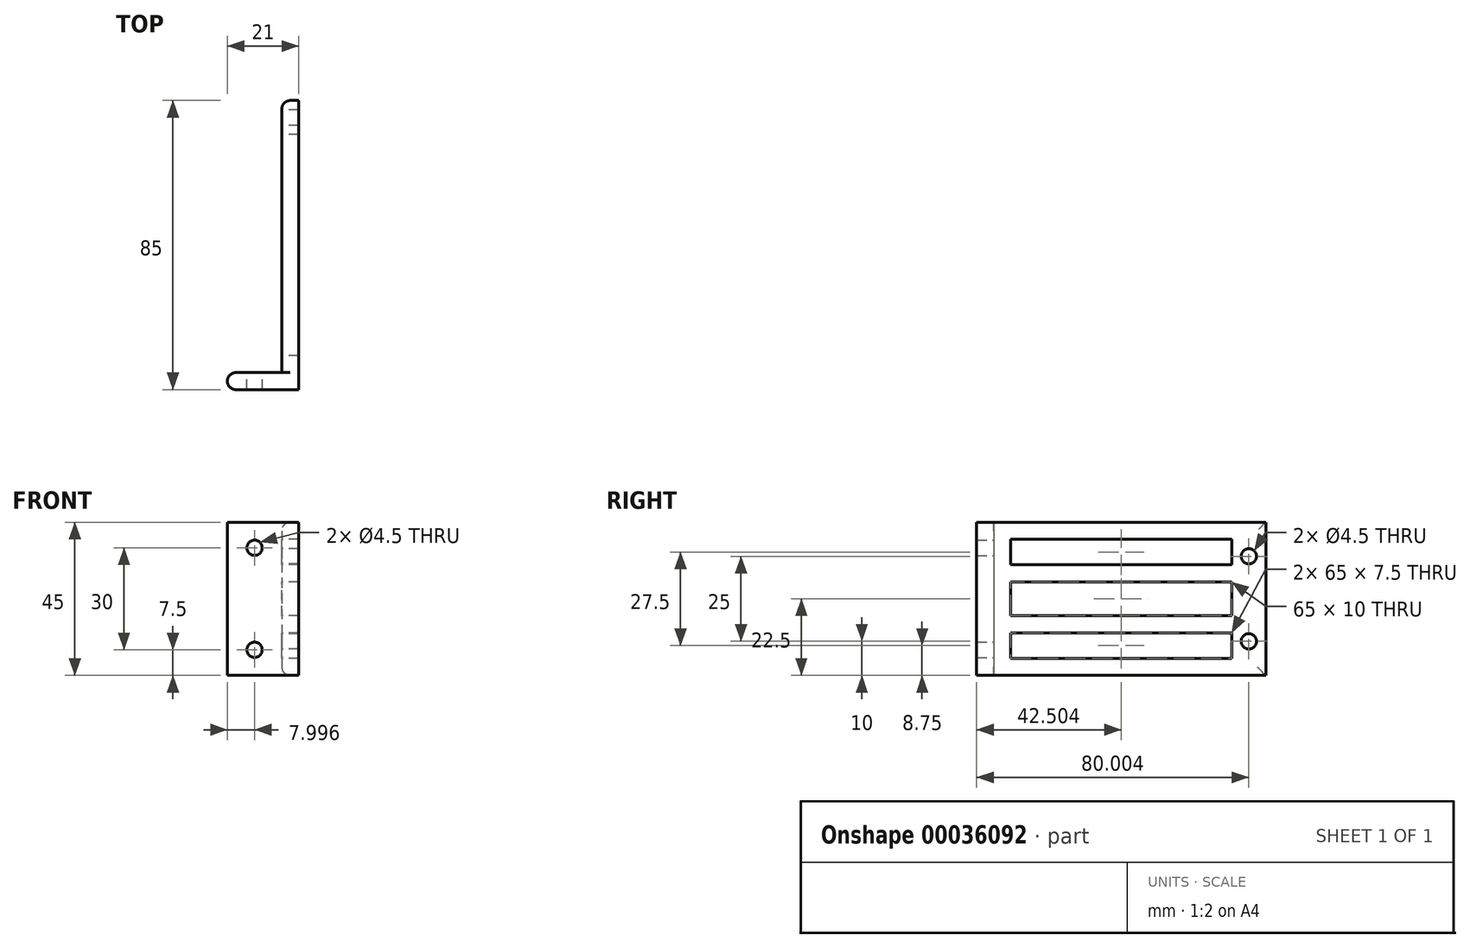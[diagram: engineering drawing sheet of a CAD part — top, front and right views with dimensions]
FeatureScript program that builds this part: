
annotation { "Feature Type Name" : "Feature", "Feature Type Description" : "" }
export const myFeature = defineFeature(function(context is Context, id is Id, definition is map)
    precondition{}
    {
        {
            var Q0;
            Q0=qCreatedBy(makeId("Top.planeOp"),FACE);
            var sketch = newSketch(context, id + "F0", { "sketchPlane" : qUnion([Q0])});
            skLineSegment(sketch, "E0.bottom", {"start": v(-20.1, -24.97) * mm, "end": v(-4.1, -24.97) * mm});
            skLineSegment(sketch, "E0.top", {"start": v(-20.1, -29.97) * mm, "end": v(-4.1, -29.97) * mm});
            skLineSegment(sketch, "E0.left", {"start": v(-20.1, -24.97) * mm, "end": v(-20.1, -29.97) * mm});
            skLineSegment(sketch, "E1", {"start": v(-4.1, -24.97) * mm, "end": v(-4.1, 55.03) * mm});
            skLineSegment(sketch, "E2", {"start": v(-4.1, -24.97) * mm, "end": v(-4.1, -29.97) * mm});
            skLineSegment(sketch, "E3", {"start": v(0.9, 55.03) * mm, "end": v(-4.1, 55.03) * mm});
            skLineSegment(sketch, "E4", {"start": v(0.9, 55.03) * mm, "end": v(0.9, -29.97) * mm});
            skLineSegment(sketch, "E5", {"start": v(0.9, -29.97) * mm, "end": v(-4.1, -29.97) * mm});
            skSolve(sketch);
        }
        {
            var Q0;
            Q0=makeQuery(id+"F0.imprint","IMPRINT",FACE,{"disambiguationData":[TD([[makeQuery(id+"F0.imprint","IMPRINT",EDGE,{"derivedFrom":sQuery(id+"F0.wireOp",EDGE,"E1")}),-1.0]])]});
            var Q1;
            Q1=makeQuery(id+"F0.imprint","IMPRINT",FACE,{"disambiguationData":[TD([[makeQuery(id+"F0.imprint","IMPRINT",EDGE,{"derivedFrom":sQuery(id+"F0.wireOp",EDGE,"cca33415-58cc-4f14-9f05-c62fcb7601cd.bottom")}),-1.0]])]});
            var Q2;
            Q2=makeQuery(id+"F0.imprint","IMPRINT",FACE,{"disambiguationData":[TD([[makeQuery(id+"F0.imprint","IMPRINT",EDGE,{"derivedFrom":sQuery(id+"F0.wireOp",EDGE,"E0.bottom")}),-1.0]])]});
            extrude(context, id + "F1", {"entities" : qUnion([Q0, Q1, Q2]), "depth" : 45 * mm});
        }
        {
            var Q0;
            Q0=makeQuery(id+"F1.opExtrude","SWEPT_FACE",FACE,{"disambiguationData":[OSD([sQuery(id+"F0.wireOp",EDGE,"E0.bottom")])]});
            var sketch = newSketch(context, id + "F2", { "sketchPlane" : qUnion([Q0])});
            skCircle(sketch, "E6", {"center": v(12.1, 7.5) * mm, "radius": 2.25 * mm});
            skCircle(sketch, "E7", {"center": v(12.1, 37.5) * mm, "radius": 2.25 * mm});
            skSolve(sketch);
        }
        {
            var Q0;
            Q0=makeQuery(id+"F2.imprint","IMPRINT",FACE,{"disambiguationData":[TD([[makeQuery(id+"F2.imprint","IMPRINT",EDGE,{"derivedFrom":sQuery(id+"F2.wireOp",EDGE,"E6")}),1.0]])]});
            var Q1;
            Q1=makeQuery(id+"F2.imprint","IMPRINT",FACE,{"disambiguationData":[TD([[makeQuery(id+"F2.imprint","IMPRINT",EDGE,{"derivedFrom":sQuery(id+"F2.wireOp",EDGE,"E7")}),1.0]])]});
            extrude(context, id + "F3", {"entities" : qUnion([Q0, Q1]), "operationType" : NewBodyOperationType.REMOVE, "endBound" : BoundingType.UP_TO_NEXT, "oppositeDirection" : true, "depth" : 25 * mm});
        }
        {
            var Q0;
            Q0=makeQuery(id+"F1.opExtrude","SWEPT_FACE",FACE,{"disambiguationData":[OSD([sQuery(id+"F0.wireOp",EDGE,"E1")])]});
            var sketch = newSketch(context, id + "F4", { "sketchPlane" : qUnion([Q0])});
            skLineSegment(sketch, "E8.bottom", {"start": v(19.97, 5) * mm, "end": v(-45.03, 5) * mm});
            skLineSegment(sketch, "E8.top", {"start": v(19.97, 40) * mm, "end": v(-45.03, 40) * mm});
            skLineSegment(sketch, "E8.left", {"start": v(19.97, 5) * mm, "end": v(19.97, 40) * mm});
            skLineSegment(sketch, "E8.right", {"start": v(-45.03, 5) * mm, "end": v(-45.03, 40) * mm});
            skCircle(sketch, "E9", {"center": v(-50.03, 10) * mm, "radius": 2.25 * mm});
            skCircle(sketch, "E10", {"center": v(-50.03, 35) * mm, "radius": 2.25 * mm});
            skLineSegment(sketch, "E11.bottom", {"start": v(-45.03, 12.5) * mm, "end": v(19.97, 12.5) * mm});
            skLineSegment(sketch, "E11.top", {"start": v(-45.03, 17.5) * mm, "end": v(19.97, 17.5) * mm});
            skLineSegment(sketch, "E11.left", {"start": v(-45.03, 12.5) * mm, "end": v(-45.03, 17.5) * mm});
            skLineSegment(sketch, "E11.right", {"start": v(19.97, 12.5) * mm, "end": v(19.97, 17.5) * mm});
            skLineSegment(sketch, "E12.bottom", {"start": v(-45.03, 27.5) * mm, "end": v(19.97, 27.5) * mm});
            skLineSegment(sketch, "E12.top", {"start": v(-45.03, 32.5) * mm, "end": v(19.97, 32.5) * mm});
            skLineSegment(sketch, "E12.left", {"start": v(-45.03, 27.5) * mm, "end": v(-45.03, 32.5) * mm});
            skLineSegment(sketch, "E12.right", {"start": v(19.97, 27.5) * mm, "end": v(19.97, 32.5) * mm});
            skSolve(sketch);
        }
        {
            var Q0;
            Q0=makeQuery(id+"F4.imprint","IMPRINT",FACE,{"disambiguationData":[TD([[makeQuery(id+"F4.imprint","IMPRINT",EDGE,{"derivedFrom":sQuery(id+"F4.wireOp",EDGE,"E8.bottom")}),-1.0]])]});
            var Q1;
            Q1=makeQuery(id+"F4.imprint","IMPRINT",FACE,{"disambiguationData":[TD([[makeQuery(id+"F4.imprint","IMPRINT",EDGE,{"derivedFrom":sQuery(id+"F4.wireOp",EDGE,"E10")}),1.0]])]});
            var Q2;
            Q2=makeQuery(id+"F4.imprint","IMPRINT",FACE,{"disambiguationData":[TD([[makeQuery(id+"F4.imprint","IMPRINT",EDGE,{"derivedFrom":sQuery(id+"F4.wireOp",EDGE,"E9")}),1.0]])]});
            var Q3;
            {var subQ1=sQuery(id+"F4.wireOp",EDGE,"E11.top");Q3=makeQuery(id+"F4.imprint","IMPRINT",FACE,{"disambiguationData":[TD([[makeQuery(id+"F4.imprint","IMPRINT",EDGE,{"derivedFrom":subQ1}),1.0]])]});}
            var Q4;
            {var subQ2=sQuery(id+"F4.wireOp",EDGE,"E8.top");Q4=makeQuery(id+"F4.imprint","IMPRINT",FACE,{"disambiguationData":[TD([[makeQuery(id+"F4.imprint","IMPRINT",EDGE,{"derivedFrom":subQ2}),1.0]])]});}
            extrude(context, id + "F5", {"entities" : qUnion([Q0, Q1, Q2, Q3, Q4]), "operationType" : NewBodyOperationType.REMOVE, "endBound" : BoundingType.UP_TO_NEXT, "oppositeDirection" : true, "depth" : 25 * mm});
        }
        {
            var Q0;
            Q0=makeQuery(id+"F1.opExtrude","CAP_EDGE",EDGE,{"disambiguationData":[OSD([sQuery(id+"F0.wireOp",EDGE,"E1")])],"isStart":true});
            var Q1;
            Q1=makeQuery(id+"F1.opExtrude","SWEPT_EDGE",EDGE,{"disambiguationData":[OSD([sQuery(id+"F0.wireOp",EDGE,"E1"),sQuery(id+"F0.wireOp",EDGE,"E3")])]});
            var Q2;
            Q2=makeQuery(id+"F1.opExtrude","CAP_EDGE",EDGE,{"disambiguationData":[OSD([sQuery(id+"F0.wireOp",EDGE,"E1")])],"isStart":false});
            var Q3;
            Q3=makeQuery(id+"F5.boolean.opBoolean","COPY",EDGE,{"derivedFrom":makeQuery(id+"F5.opExtrude","CAP_EDGE",EDGE,{"disambiguationData":[OSD([sQuery(id+"F4.wireOp",EDGE,"E8.right")])],"isStart":true})});
            var Q4;
            Q4=makeQuery(id+"F5.boolean.opBoolean","COPY",EDGE,{"derivedFrom":makeQuery(id+"F5.opExtrude","CAP_EDGE",EDGE,{"disambiguationData":[OSD([sQuery(id+"F4.wireOp",EDGE,"E8.left")])],"isStart":true})});
            var Q5;
            Q5=makeQuery(id+"F1.opExtrude","SWEPT_EDGE",EDGE,{"disambiguationData":[OSD([sQuery(id+"F0.wireOp",EDGE,"E0.bottom"),sQuery(id+"F0.wireOp",EDGE,"E0.left")])]});
            var Q6;
            Q6=makeQuery(id+"F1.opExtrude","SWEPT_EDGE",EDGE,{"disambiguationData":[OSD([sQuery(id+"F0.wireOp",EDGE,"E0.top"),sQuery(id+"F0.wireOp",EDGE,"E0.left")])]});
            fillet(context, id + "F6", {"entities" : qUnion([Q0, Q1, Q2, Q3, Q4, Q5, Q6]), "radius" : 2.5 * mm, "tangentPropagation" : true, "allowEdgeOverflow" : false});
        }
    });
